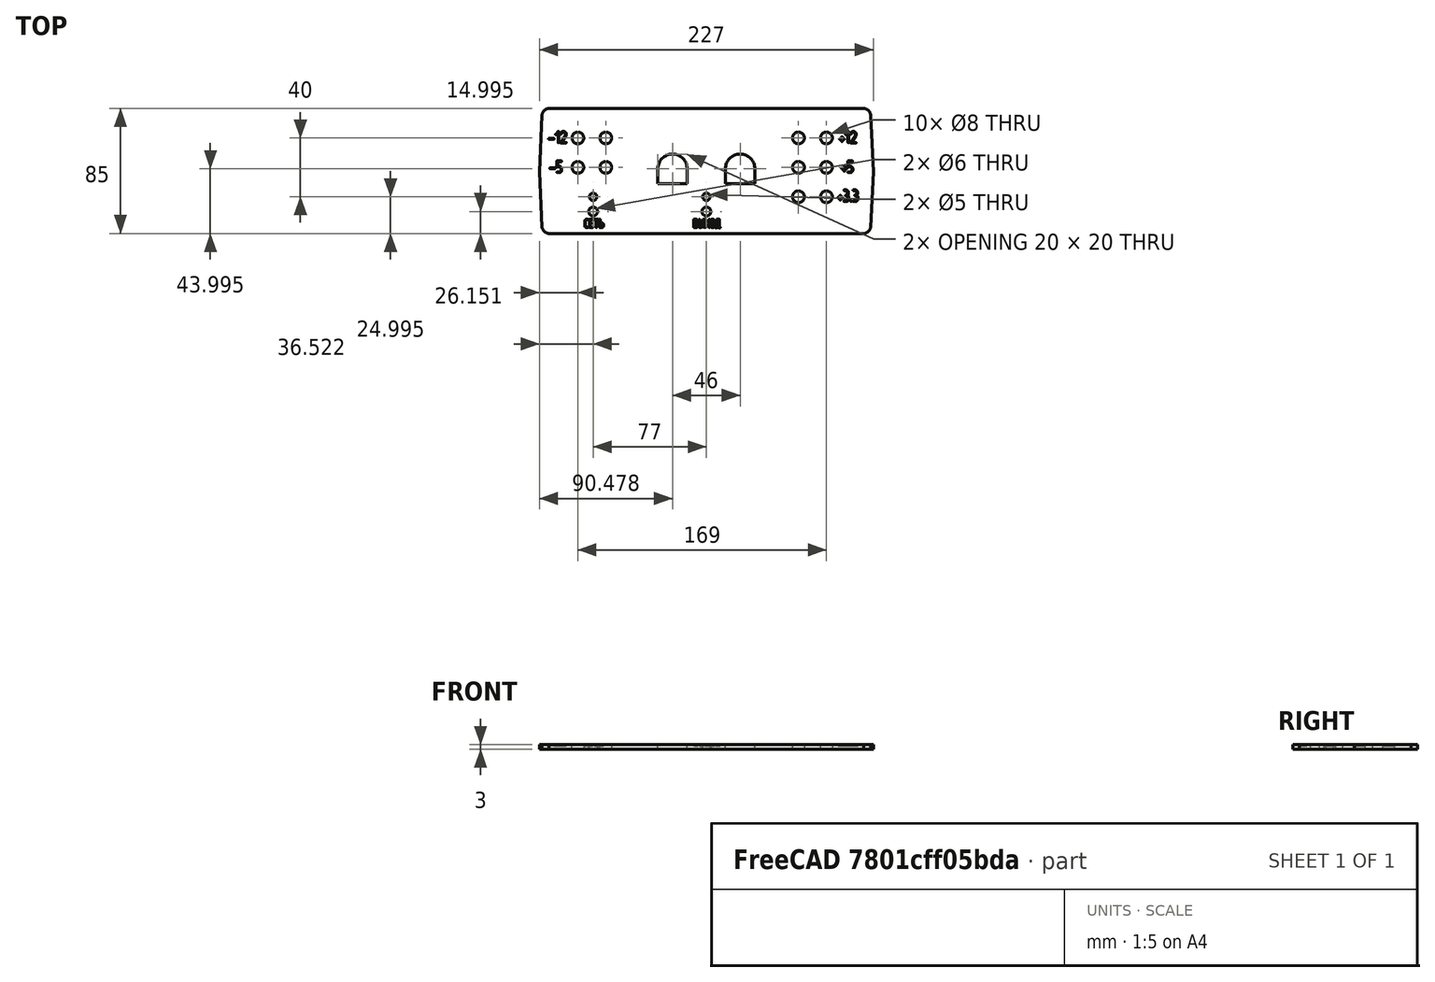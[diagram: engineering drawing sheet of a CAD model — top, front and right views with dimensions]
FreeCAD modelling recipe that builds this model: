
FCSTD DOCUMENT  (FreeCAD 0.20R)
Label: kradex-z17-front-panel
License: All rights reserved
LicenseURL: http://en.wikipedia.org/wiki/All_rights_reserved
objects: Part::Feature×17, Part::Extrusion×8, Part::Part2DObjectPython×7, Part::Cut×7, Sketcher::SketchObject×1
note: 40 computed .brp shape members not serialized (recipe doc carries the construction recipe); baked Part::Feature solids carry a one-line shape summary decoded from their .brp

FEATURE [Part::Feature] Wire
  shape: bbox 227 x 85 x 2e-07 mm, 0 faces, 0 solids (baked)
FEATURE [Part::Feature] Wire001
  shape: bbox 20 x 20 x 2e-07 mm, 0 faces, 0 solids (baked)
FEATURE [Part::Feature] Wire002
  shape: bbox 20 x 20 x 2e-07 mm, 0 faces, 0 solids (baked)
FEATURE [Part::Feature] Wire003
  shape: bbox 5 x 5 x 2e-07 mm, 0 faces, 0 solids (baked)
FEATURE [Part::Feature] Wire004
  shape: bbox 6 x 6 x 2e-07 mm, 0 faces, 0 solids (baked)
FEATURE [Part::Feature] Wire005
  shape: bbox 6 x 6 x 2e-07 mm, 0 faces, 0 solids (baked)
FEATURE [Part::Feature] Wire006
  shape: bbox 5 x 5 x 2e-07 mm, 0 faces, 0 solids (baked)
FEATURE [Part::Feature] Wire007 .. Wire016  x10 (patterned run collapsed; names and placements below)
  shape: bbox 8 x 8 x 2e-07 mm, 0 faces, 0 solids (baked)
FEATURE [Sketcher::SketchObject] Sketch
  FullyConstrained = false
  sketch-geometry (32):
    g0: LineSegment StartX=16.3264 StartY=11 StartZ=0 EndX=230.4 EndY=11 EndZ=0
    g1: ArcOfCircle CenterX=230.091 CenterY=15.9905 CenterZ=0 NormalX=0 NormalY=0 NormalZ=1 AngleXU=0 Radius=5 StartAngle=4.77411 EndAngle=6.18399
    g2: LineSegment StartX=235.067 StartY=15.4953 StartZ=0 EndX=236.853 EndY=53 EndZ=0
    g3: LineSegment StartX=236.853 StartY=53 StartZ=0 EndX=235.062 EndY=91.4947 EndZ=0
    g4: ArcOfCircle CenterX=230.086 CenterY=91.0055 CenterZ=0 NormalX=0 NormalY=0 NormalZ=1 AngleXU=0 Radius=5 StartAngle=0.0980037 EndAngle=1.52407
    g5: LineSegment StartX=230.32 StartY=96 StartZ=0 EndX=16.3702 EndY=96 EndZ=0
    g6: ArcOfCircle CenterX=16.6213 CenterY=91.0063 CenterZ=0 NormalX=0 NormalY=0 NormalZ=1 AngleXU=0 Radius=5 StartAngle=1.62103 EndAngle=3.05278
    g7: LineSegment StartX=11.641 StartY=91.4498 StartZ=0 EndX=9.8526 EndY=53 EndZ=0
    g8: LineSegment StartX=9.8526 StartY=53 StartZ=0 EndX=11.64 EndY=15.4641 EndZ=0
    g9: ArcOfCircle CenterX=16.6121 CenterY=15.9918 CenterZ=0 NormalX=0 NormalY=0 NormalZ=1 AngleXU=0 Radius=5 StartAngle=3.24733 EndAngle=4.65521
    g10: LineSegment StartX=90.3264 StartY=45 StartZ=0 EndX=90.3264 EndY=55 EndZ=0
    g11: ArcOfCircle CenterX=100.326 CenterY=55 CenterZ=0 NormalX=0 NormalY=0 NormalZ=1 AngleXU=0 Radius=10 StartAngle=0 EndAngle=3.14159
    g12: LineSegment StartX=110.326 StartY=55 StartZ=0 EndX=110.326 EndY=45 EndZ=0
    g13: LineSegment StartX=110.326 StartY=45 StartZ=0 EndX=90.3264 EndY=45 EndZ=0
    g14: LineSegment StartX=156.326 StartY=45 StartZ=0 EndX=136.326 EndY=45 EndZ=0
    g15: LineSegment StartX=136.326 StartY=45 StartZ=0 EndX=136.326 EndY=55 EndZ=0
    g16: ArcOfCircle CenterX=146.326 CenterY=55 CenterZ=0 NormalX=0 NormalY=0 NormalZ=1 AngleXU=0 Radius=10 StartAngle=0 EndAngle=3.14159
    g17: LineSegment StartX=156.326 StartY=55 StartZ=0 EndX=156.326 EndY=45 EndZ=0
    g18: Circle CenterX=123.37 CenterY=36 CenterZ=0 NormalX=0 NormalY=0 NormalZ=-1 AngleXU=0 Radius=2.5
    g19: Circle CenterX=123.37 CenterY=26 CenterZ=0 NormalX=0 NormalY=0 NormalZ=-1 AngleXU=0 Radius=3
    g20: Circle CenterX=46.3702 CenterY=26 CenterZ=0 NormalX=0 NormalY=0 NormalZ=-1 AngleXU=0 Radius=3
    g21: Circle CenterX=46.3702 CenterY=36 CenterZ=0 NormalX=0 NormalY=0 NormalZ=-1 AngleXU=0 Radius=2.5
    g22: Circle CenterX=36 CenterY=76 CenterZ=0 NormalX=0 NormalY=0 NormalZ=-1 AngleXU=0 Radius=4
    g23: Circle CenterX=55 CenterY=76 CenterZ=0 NormalX=0 NormalY=0 NormalZ=-1 AngleXU=0 Radius=4
    g24: Circle CenterX=55 CenterY=56 CenterZ=0 NormalX=0 NormalY=0 NormalZ=-1 AngleXU=0 Radius=4
    g25: Circle CenterX=36 CenterY=56 CenterZ=0 NormalX=0 NormalY=0 NormalZ=-1 AngleXU=0 Radius=4
    g26: Circle CenterX=205 CenterY=76 CenterZ=0 NormalX=0 NormalY=0 NormalZ=-1 AngleXU=0 Radius=4
    g27: Circle CenterX=186 CenterY=76 CenterZ=0 NormalX=0 NormalY=0 NormalZ=-1 AngleXU=0 Radius=4
    g28: Circle CenterX=205 CenterY=56 CenterZ=0 NormalX=0 NormalY=0 NormalZ=-1 AngleXU=0 Radius=4
    g29: Circle CenterX=186 CenterY=56 CenterZ=0 NormalX=0 NormalY=0 NormalZ=-1 AngleXU=0 Radius=4
    g30: Circle CenterX=205 CenterY=36 CenterZ=0 NormalX=0 NormalY=0 NormalZ=-1 AngleXU=0 Radius=4
    g31: Circle CenterX=186 CenterY=36 CenterZ=0 NormalX=0 NormalY=0 NormalZ=-1 AngleXU=0 Radius=4
  constraints (25):
    c: Coincident(g0,g1)
    c: Coincident(g1,g2)
    c: Coincident(g2,g3)
    c: Coincident(g3,g4)
    c: Coincident(g4,g5)
    c: Horizontal(g5)
    c: Coincident(g5,g6)
    c: Coincident(g6,g7)
    c: Coincident(g7,g8)
    c: Coincident(g8,g9)
    c: Coincident(g9,g0)
    c: Vertical(g10)
    c: Coincident(g10,g11)
    c: Coincident(g11,g12)
    c: Vertical(g12)
    c: Coincident(g12,g13)
    c: Horizontal(g13)
    c: Coincident(g13,g10)
    c: Horizontal(g14)
    c: Coincident(g14,g15)
    c: Vertical(g15)
    c: Coincident(g15,g16)
    c: Coincident(g16,g17)
    c: Vertical(g17)
    c: Coincident(g17,g14)
FEATURE [Part::Extrusion] Extrude
  Base = -> Sketch
  Dir = (0,0,1)
  DirMode = 2
  FaceMakerClass = Part::FaceMakerBullseye
  LengthFwd = 3
  LengthRev = 0
  Placement = pos=(-59.8885,-61.0947,0) rot=(0,0,1;0rad)
  Solid = true
  Symmetric = false
FEATURE [Part::Part2DObjectPython] ShapeString  label="-12"  # Draft 2D object (typed FeaturePython)
  FontFile = <userpath>/.fonts/gost_type_a.ttf
  MakeFace = true
  Placement = pos=(-44.1237,11.4241,3.1) rot=(0,0,1;0rad)
  Size = 7
  String = -12
  Tracking = 0
FEATURE [Part::Part2DObjectPython] ShapeString001  label="-5"  # Draft 2D object (typed FeaturePython)
  FontFile = <userpath>/.fonts/gost_type_a.ttf
  MakeFace = true
  Placement = pos=(-43.3524,-8.62825,3.1) rot=(0,0,1;0rad)
  Size = 7
  String = -5
  Tracking = 0
FEATURE [Part::Part2DObjectPython] ShapeString002  label="+12"  # Draft 2D object (typed FeaturePython)
  FontFile = <userpath>/.fonts/gost_type_a.ttf
  MakeFace = true
  Placement = pos=(153.701,11.4241,3.1) rot=(0,0,1;0rad)
  Size = 7
  String = +12
  Tracking = 0
FEATURE [Part::Part2DObjectPython] ShapeString003  label="+5"  # Draft 2D object (typed FeaturePython)
  FontFile = <userpath>/.fonts/gost_type_a.ttf
  MakeFace = true
  Placement = pos=(155.243,-8.62825,3.1) rot=(0,0,1;0rad)
  Size = 7
  String = +5
  Tracking = 0
FEATURE [Part::Part2DObjectPython] ShapeString004  label="+3.3"  # Draft 2D object (typed FeaturePython)
  FontFile = <userpath>/.fonts/gost_type_a.ttf
  MakeFace = true
  Placement = pos=(152.544,-28.295,3.1) rot=(0,0,1;0rad)
  Size = 7
  String = +3.3
  Tracking = 0
FEATURE [Part::Part2DObjectPython] ShapeString005  label="Сеть"  # Draft 2D object (typed FeaturePython)
  FontFile = <userpath>/.fonts/gost_type_a.ttf
  MakeFace = true
  Placement = pos=(-19.67,-46,3.1) rot=(0,0,1;0rad)
  Size = 5
  String = СЕТЬ
  Tracking = 0
FEATURE [Part::Part2DObjectPython] ShapeString006  label="Выход"  # Draft 2D object (typed FeaturePython)
  FontFile = <userpath>/.fonts/gost_type_a.ttf
  MakeFace = true
  Placement = pos=(54.53,-46,3.1) rot=(0,0,1;0rad)
  Size = 5
  String = ВЫХОД
  Tracking = 0
FEATURE [Part::Extrusion] Extrude001
  Base = -> ShapeString
  Dir = (0,0,1)
  DirMode = 2
  FaceMakerClass = Part::FaceMakerBullseye
  LengthFwd = 1
  LengthRev = 0
  Reversed = true
  Solid = false
  Symmetric = false
FEATURE [Part::Extrusion] Extrude002
  Base = -> ShapeString001
  Dir = (0,0,1)
  DirMode = 2
  FaceMakerClass = Part::FaceMakerBullseye
  LengthFwd = 1
  LengthRev = 0
  Reversed = true
  Solid = false
  Symmetric = false
FEATURE [Part::Extrusion] Extrude003
  Base = -> ShapeString002
  Dir = (0,0,1)
  DirMode = 2
  FaceMakerClass = Part::FaceMakerBullseye
  LengthFwd = 1
  LengthRev = 0
  Reversed = true
  Solid = false
  Symmetric = false
FEATURE [Part::Extrusion] Extrude004
  Base = -> ShapeString003
  Dir = (0,0,1)
  DirMode = 2
  FaceMakerClass = Part::FaceMakerBullseye
  LengthFwd = 1
  LengthRev = 0
  Reversed = true
  Solid = false
  Symmetric = false
FEATURE [Part::Extrusion] Extrude005
  Base = -> ShapeString004
  Dir = (0,0,1)
  DirMode = 2
  FaceMakerClass = Part::FaceMakerBullseye
  LengthFwd = 1
  LengthRev = 0
  Reversed = true
  Solid = false
  Symmetric = false
FEATURE [Part::Extrusion] Extrude006
  Base = -> ShapeString005
  Dir = (0,0,1)
  DirMode = 2
  FaceMakerClass = Part::FaceMakerBullseye
  LengthFwd = 1
  LengthRev = 0
  Reversed = true
  Solid = false
  Symmetric = false
FEATURE [Part::Extrusion] Extrude007
  Base = -> ShapeString006
  Dir = (0,0,1)
  DirMode = 2
  FaceMakerClass = Part::FaceMakerBullseye
  LengthFwd = 1
  LengthRev = 0
  Reversed = true
  Solid = false
  Symmetric = false
FEATURE [Part::Cut] Cut
  Base = -> Extrude
  Tool = -> Extrude001
FEATURE [Part::Cut] Cut001
  Base = -> Cut
  Tool = -> Extrude002
FEATURE [Part::Cut] Cut002
  Base = -> Cut001
  Tool = -> Extrude003
FEATURE [Part::Cut] Cut003
  Base = -> Cut002
  Tool = -> Extrude004
FEATURE [Part::Cut] Cut004
  Base = -> Cut003
  Tool = -> Extrude005
FEATURE [Part::Cut] Cut005
  Base = -> Cut004
  Tool = -> Extrude006
FEATURE [Part::Cut] Cut006
  Base = -> Cut005
  Tool = -> Extrude007
